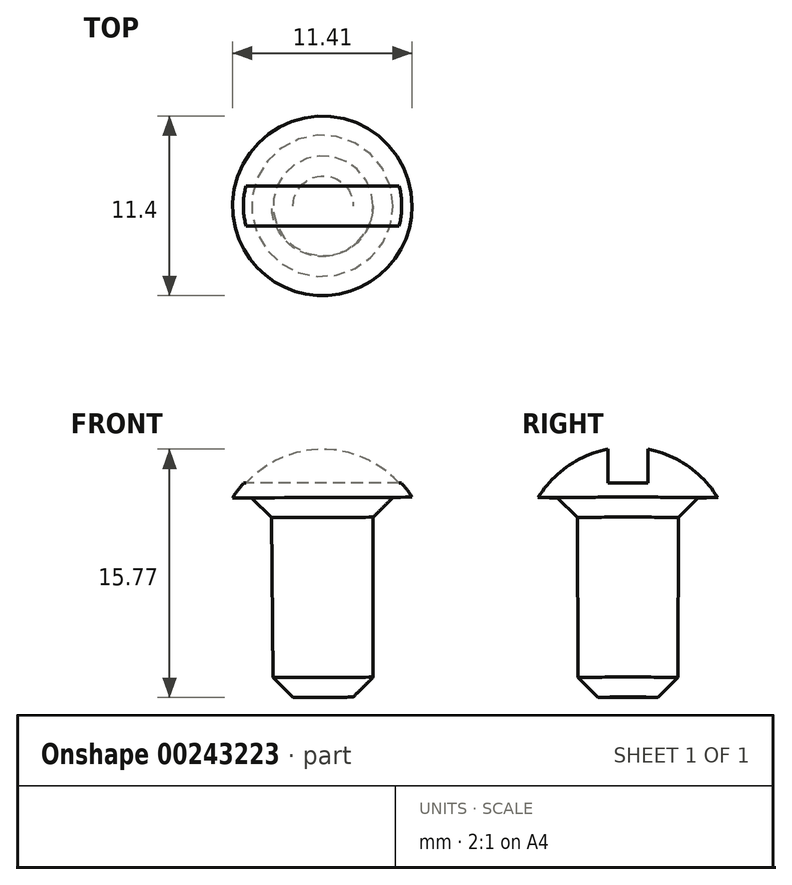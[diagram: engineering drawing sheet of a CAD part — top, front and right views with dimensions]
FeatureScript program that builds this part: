
annotation { "Feature Type Name" : "Feature", "Feature Type Description" : "" }
export const myFeature = defineFeature(function(context is Context, id is Id, definition is map)
    precondition{}
    {
        {
            var Q0;
            Q0=qCreatedBy(makeId("Front.planeOp"),FACE);
            var sketch = newSketch(context, id + "F0", { "sketchPlane" : qUnion([Q0])});
            skArc(sketch, "E0", {"start": v(5.71, 3.56) * mm, "mid": v(3.27, 5.88) * mm, "end": v(0, 6.73) * mm});
            skLineSegment(sketch, "E1.bottom", {"start": v(3.24, -9.14) * mm, "end": v(0.06, -9.14) * mm});
            skLineSegment(sketch, "E1.top", {"start": v(5.71, 3.56) * mm, "end": v(3.24, 3.56) * mm});
            skLineSegment(sketch, "E2.bottom", {"start": v(0.06, -9.14) * mm, "end": v(3.24, -9.14) * mm});
            skLineSegment(sketch, "E2.right", {"start": v(3.24, -9.14) * mm, "end": v(3.24, 3.56) * mm});
            skLineSegment(sketch, "E3", {"start": v(0, 6.73) * mm, "end": v(0.06, -9.14) * mm});
            skPoint(sketch, "E1.right.end.orphan", {"position": v(-5.72, 3.56) * mm});
            skSolve(sketch);
        }
        {
            var Q0;
            Q0 = qSketchRegion(id + "F0", true);
            var Q1;
            Q1=sQuery(id+"F0.wireOp",EDGE,"E3");
            revolve(context, id + "F1", {"entities" : qUnion([Q0]), "axis" : qUnion([Q1]), "revolveType" : RevolveType.FULL});
        }
        {
            var Q0;
            Q0=makeQuery(id+"F1.opRevolve","SWEPT_EDGE",EDGE,{"disambiguationData":[OSD([sQuery(id+"F0.wireOp",EDGE,"E2.bottom"),sQuery(id+"F0.wireOp",EDGE,"E2.right")])]});
            chamfer(context, id + "F2", {"entities" : qUnion([Q0]), "width" : 1.27 * mm, "tangentPropagation" : true});
        }
        {
            var Q0;
            Q0=qCreatedBy(makeId("Top.planeOp"),FACE);
            var sketch = newSketch(context, id + "F3", { "sketchPlane" : qUnion([Q0])});
            skLineSegment(sketch, "E4.bottom", {"start": v(5.08, 1.27) * mm, "end": v(-5.08, 1.27) * mm});
            skLineSegment(sketch, "E4.top", {"start": v(5.08, -1.27) * mm, "end": v(-5.08, -1.27) * mm});
            skLineSegment(sketch, "E4.left", {"start": v(5.08, 1.27) * mm, "end": v(5.08, -1.27) * mm});
            skLineSegment(sketch, "E4.right", {"start": v(-5.08, 1.27) * mm, "end": v(-5.08, -1.27) * mm});
            skPoint(sketch, "E4.middle", {"position": v(0, 0) * mm});
            skSolve(sketch);
        }
        {
            var Q0;
            Q0 = qSketchRegion(id + "F3", true);
            extrude(context, id + "F4", {"entities" : qUnion([Q0]), "operationType" : NewBodyOperationType.REMOVE, "depth" : 25.4 * mm, "hasSecondDirection" : true, "secondDirectionOppositeDirection" : false, "secondDirectionDepth" : 4.44 * mm});
        }
    });
